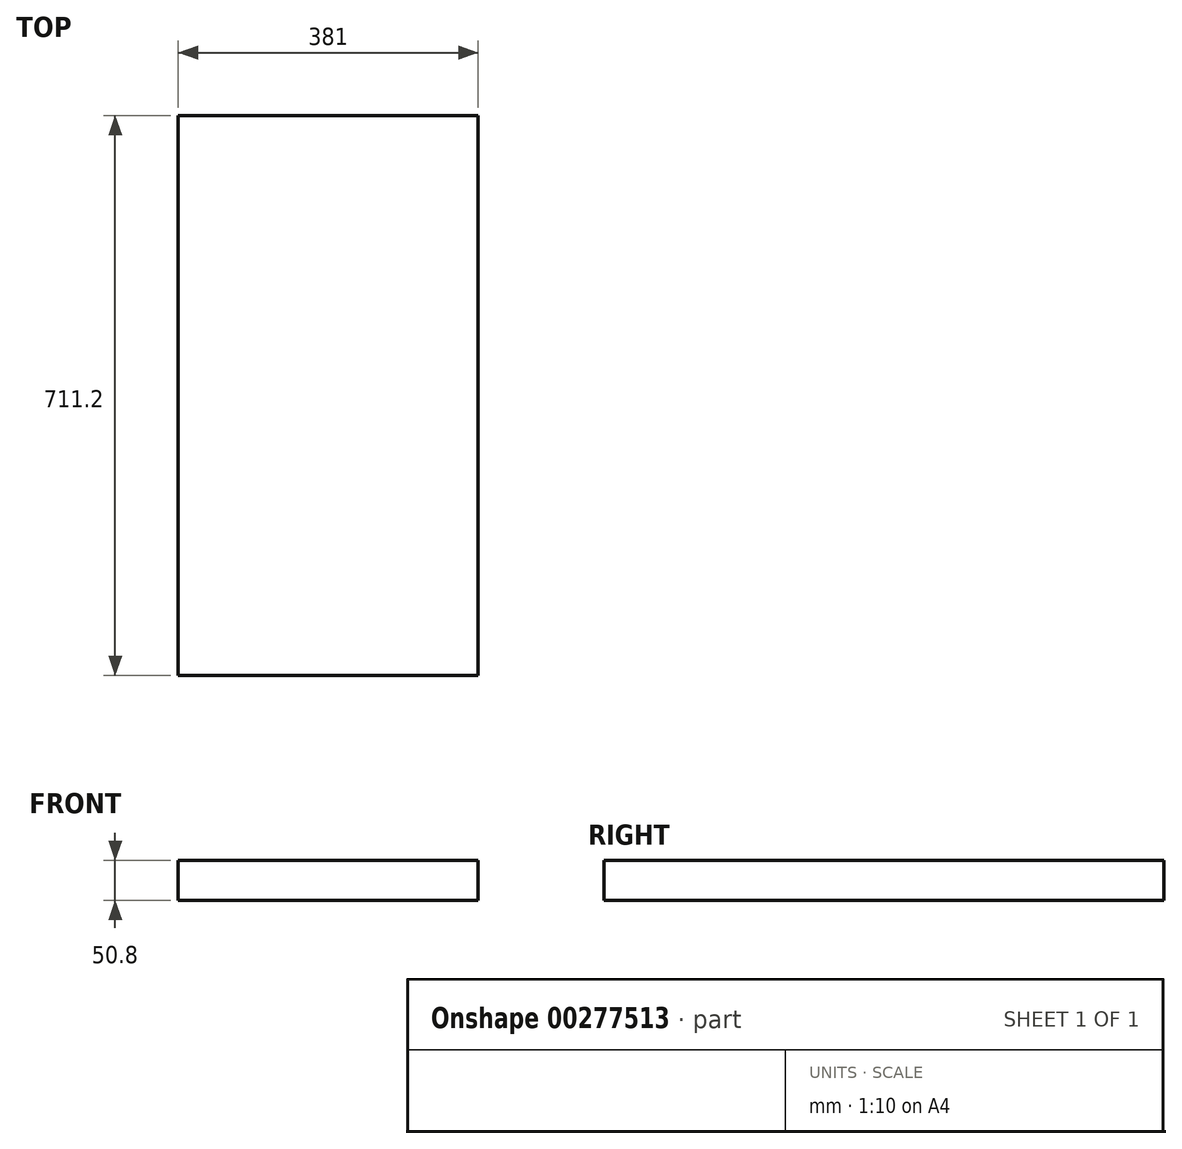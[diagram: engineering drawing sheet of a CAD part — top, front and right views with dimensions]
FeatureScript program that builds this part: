
annotation { "Feature Type Name" : "Feature", "Feature Type Description" : "" }
export const myFeature = defineFeature(function(context is Context, id is Id, definition is map)
    precondition{}
    {
        {
            var Q0;
            Q0=qCreatedBy(makeId("Top.planeOp"),FACE);
            var sketch = newSketch(context, id + "F0", { "sketchPlane" : qUnion([Q0])});
            skLineSegment(sketch, "E0.bottom", {"start": v(-190.5, 355.6) * mm, "end": v(190.5, 355.6) * mm});
            skLineSegment(sketch, "E0.top", {"start": v(-190.5, -355.6) * mm, "end": v(190.5, -355.6) * mm});
            skLineSegment(sketch, "E0.left", {"start": v(-190.5, 355.6) * mm, "end": v(-190.5, -355.6) * mm});
            skLineSegment(sketch, "E0.right", {"start": v(190.5, 355.6) * mm, "end": v(190.5, -355.6) * mm});
            skPoint(sketch, "E0.middle", {"position": v(0, 0) * mm});
            skSolve(sketch);
        }
        {
            var Q0;
            Q0=makeQuery(id+"F0.imprint","IMPRINT",FACE,{"disambiguationData":[TD([[makeQuery(id+"F0.imprint","IMPRINT",EDGE,{"derivedFrom":sQuery(id+"F0.wireOp",EDGE,"E0.bottom")}),-1.0]])]});
            extrude(context, id + "F1", {"entities" : qUnion([Q0]), "depth" : 50.8 * mm});
        }
    });
